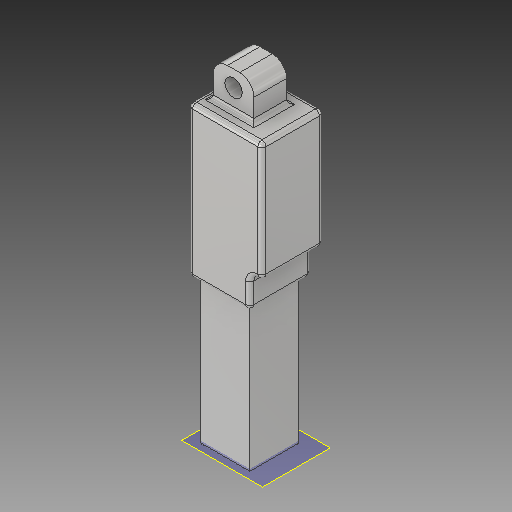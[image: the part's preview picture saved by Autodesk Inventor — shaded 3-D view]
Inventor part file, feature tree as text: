
AUTODESK INVENTOR PART (.ipt)
format: ipt  version: 2019 (Build 230136000, 136)  size: 139,264 bytes
history: mixed  units: in
note: dims shown in document units (in); Inventor stores cm internally (conversion verified against a paired STEP export)
features: other x1, extrude x1, sketch x1, imported_body x1
ambient origin geometry x8: Origin, YZ Plane, XZ Plane, XY Plane, X Axis, Y Axis, Z Axis, Center Point
bodies: Solid1 (imported_parasolid), Body (imported_parasolid)
feature tree (4):
  other  "Płaszczyzna konstrukcyjna1"
  extrude  "Wyciągnięcie proste1"  Depth=0.0394in TaperAngle=0.0deg
  sketch  "Szkic1"
  imported_body  NMx_Import_Brep_tag  [imported B-rep: ~58 faces, bbox_mm=[18.0, 81.9, 15.1]]
